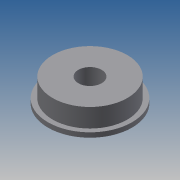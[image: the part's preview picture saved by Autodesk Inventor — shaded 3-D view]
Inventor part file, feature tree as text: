
AUTODESK INVENTOR PART (.ipt)
format: ipt  version: 2013 (Build 170138000, 138)  size: 85,504 bytes
history: native  units: mm
features: extrude x3, sketch x3
ambient origin geometry x8: Origin, YZ Plane, XZ Plane, XY Plane, X Axis, Y Axis, Z Axis, Center Point
bodies: Solid1 (feature_tree)
feature tree (6):
  extrude  "Extrusion1"  Depth=1.0mm TaperAngle=0.0deg
  extrude  "Extrusion2"  Depth=4.0mm TaperAngle=0.0deg
  extrude  "Extrusion3"  Depth=4.0mm TaperAngle=0.0deg
  sketch  "Sketch1"  dims[d0=18.0mm d2=1.0mm d3=0.0mm]
  sketch  "Sketch2"  dims[d4=16.0mm d6=4.0mm d7=0.0mm]
  sketch  "Sketch3"  dims[d8=5.0mm d10=4.0mm d11=0.0mm]
